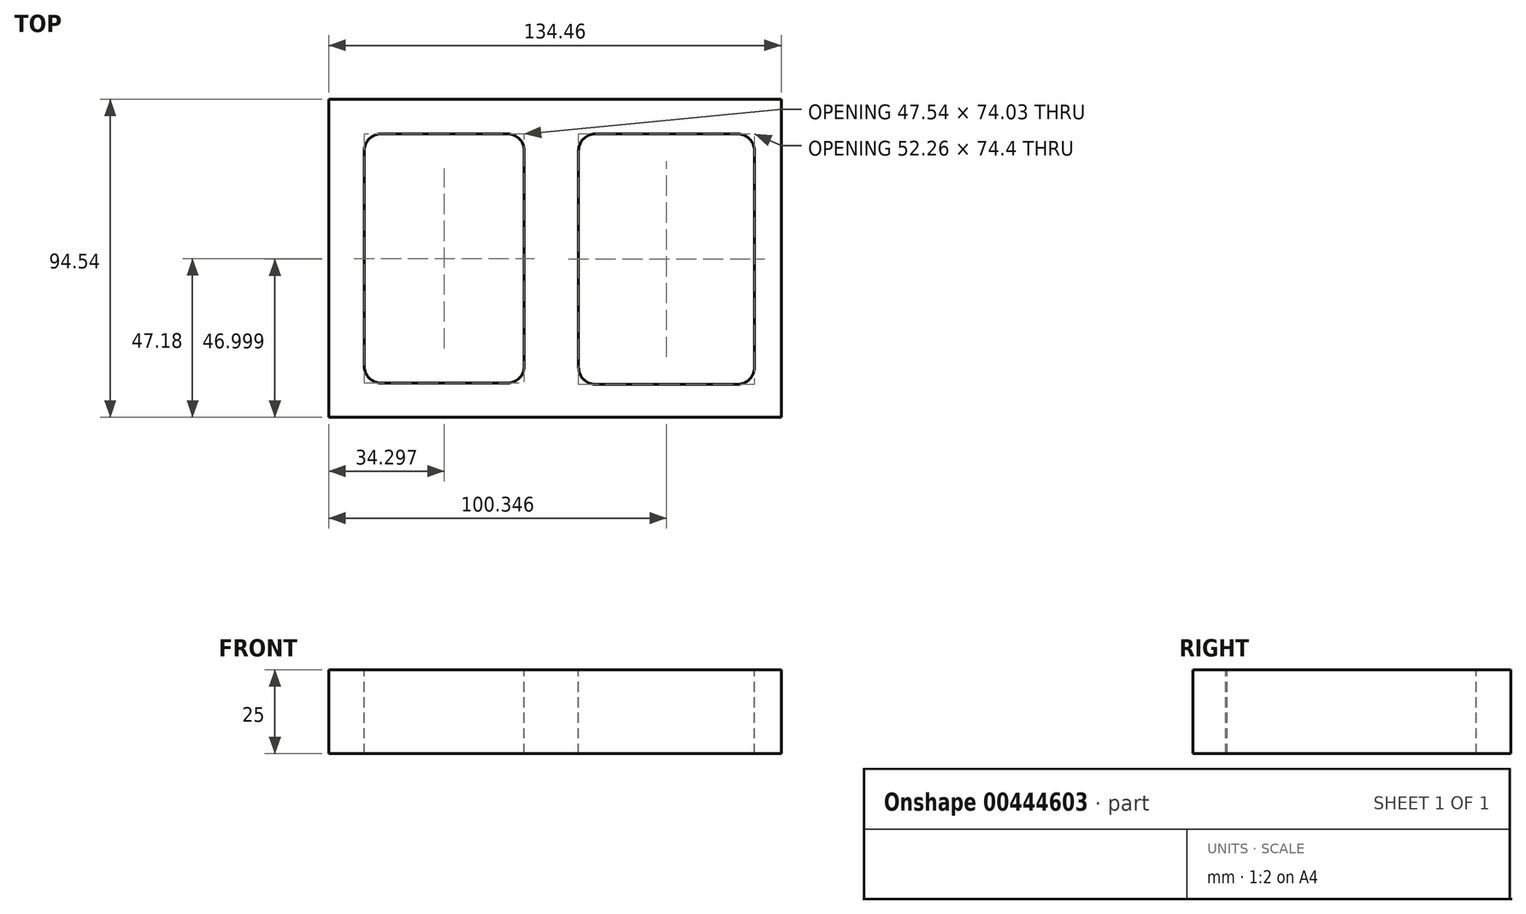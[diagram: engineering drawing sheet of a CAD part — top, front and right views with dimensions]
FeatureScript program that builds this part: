
annotation { "Feature Type Name" : "Feature", "Feature Type Description" : "" }
export const myFeature = defineFeature(function(context is Context, id is Id, definition is map)
    precondition{}
    {
        {
            var Q0;
            Q0=qCreatedBy(makeId("Top.planeOp"),FACE);
            var sketch = newSketch(context, id + "F0", { "sketchPlane" : qUnion([Q0])});
            skLineSegment(sketch, "E0.bottom", {"start": v(-67.14, 47.36) * mm, "end": v(67.32, 47.36) * mm});
            skLineSegment(sketch, "E0.top", {"start": v(-67.14, -47.18) * mm, "end": v(67.32, -47.18) * mm});
            skLineSegment(sketch, "E0.left", {"start": v(-67.14, 47.36) * mm, "end": v(-67.14, -47.18) * mm});
            skLineSegment(sketch, "E0.right", {"start": v(67.32, 47.36) * mm, "end": v(67.32, -47.18) * mm});
            skSolve(sketch);
        }
        {
            var Q0;
            Q0=makeQuery(id+"F0.imprint","IMPRINT",FACE,{"disambiguationData":[TD([[makeQuery(id+"F0.imprint","IMPRINT",EDGE,{"derivedFrom":sQuery(id+"F0.wireOp",EDGE,"E0.bottom")}),-1.0]])]});
            extrude(context, id + "F1", {"entities" : qUnion([Q0]), "depth" : 25 * mm});
        }
        {
            var Q0;
            Q0=makeQuery(id+"F1.opExtrude","CAP_FACE",FACE,{"disambiguationData":[OSD([sQuery(id+"F0.wireOp",EDGE,"E0.bottom"),sQuery(id+"F0.wireOp",EDGE,"E0.top"),sQuery(id+"F0.wireOp",EDGE,"E0.left"),sQuery(id+"F0.wireOp",EDGE,"E0.right")])],"isStart":false});
            var sketch = newSketch(context, id + "F2", { "sketchPlane" : qUnion([Q0])});
            skLineSegment(sketch, "E1.bottom", {"start": v(-56.61, 37.02) * mm, "end": v(-9.07, 37.02) * mm});
            skLineSegment(sketch, "E1.top", {"start": v(-56.61, -37.02) * mm, "end": v(-9.07, -37.02) * mm});
            skLineSegment(sketch, "E1.left", {"start": v(-56.61, 37.02) * mm, "end": v(-56.61, -37.02) * mm});
            skLineSegment(sketch, "E1.right", {"start": v(-9.07, 37.02) * mm, "end": v(-9.07, -37.02) * mm});
            skLineSegment(sketch, "E2.bottom", {"start": v(7.08, 37.02) * mm, "end": v(59.33, 37.02) * mm});
            skLineSegment(sketch, "E2.top", {"start": v(7.08, -37.38) * mm, "end": v(59.33, -37.38) * mm});
            skLineSegment(sketch, "E2.left", {"start": v(7.08, 37.02) * mm, "end": v(7.08, -37.38) * mm});
            skLineSegment(sketch, "E2.right", {"start": v(59.33, 37.02) * mm, "end": v(59.33, -37.38) * mm});
            skSolve(sketch);
        }
        {
            var Q0;
            Q0=makeQuery(id+"F2.imprint","IMPRINT",FACE,{"disambiguationData":[TD([[makeQuery(id+"F2.imprint","IMPRINT",EDGE,{"derivedFrom":sQuery(id+"F2.wireOp",EDGE,"E1.bottom")}),-1.0]])]});
            extrude(context, id + "F3", {"entities" : qUnion([Q0]), "operationType" : NewBodyOperationType.REMOVE, "oppositeDirection" : true, "depth" : 25 * mm});
        }
        {
            var Q0;
            Q0 = qSketchRegion(id + "F2", true);
            extrude(context, id + "F4", {"entities" : qUnion([Q0]), "operationType" : NewBodyOperationType.REMOVE, "oppositeDirection" : true, "depth" : 25 * mm});
        }
        {
            var Q0;
            Q0=makeQuery(id+"F3.boolean.opBoolean","COPY",EDGE,{"derivedFrom":makeQuery(id+"F3.opExtrude","SWEPT_EDGE",EDGE,{"disambiguationData":[OSD([sQuery(id+"F2.wireOp",EDGE,"E1.bottom"),sQuery(id+"F2.wireOp",EDGE,"E1.left")])]})});
            var Q1;
            Q1=makeQuery(id+"F3.boolean.opBoolean","COPY",EDGE,{"derivedFrom":makeQuery(id+"F3.opExtrude","SWEPT_EDGE",EDGE,{"disambiguationData":[OSD([sQuery(id+"F2.wireOp",EDGE,"E1.bottom"),sQuery(id+"F2.wireOp",EDGE,"E1.right")])]})});
            var Q2;
            Q2=makeQuery(id+"F3.boolean.opBoolean","COPY",EDGE,{"derivedFrom":makeQuery(id+"F3.opExtrude","SWEPT_EDGE",EDGE,{"disambiguationData":[OSD([sQuery(id+"F2.wireOp",EDGE,"E1.top"),sQuery(id+"F2.wireOp",EDGE,"E1.left")])]})});
            var Q3;
            Q3=makeQuery(id+"F3.boolean.opBoolean","COPY",EDGE,{"derivedFrom":makeQuery(id+"F3.opExtrude","SWEPT_EDGE",EDGE,{"disambiguationData":[OSD([sQuery(id+"F2.wireOp",EDGE,"E1.top"),sQuery(id+"F2.wireOp",EDGE,"E1.right")])]})});
            var Q4;
            Q4=makeQuery(id+"F4.boolean.opBoolean","COPY",EDGE,{"derivedFrom":makeQuery(id+"F4.opExtrude","SWEPT_EDGE",EDGE,{"disambiguationData":[OSD([sQuery(id+"F2.wireOp",EDGE,"E2.top"),sQuery(id+"F2.wireOp",EDGE,"E2.left")])]})});
            var Q5;
            Q5=makeQuery(id+"F4.boolean.opBoolean","COPY",EDGE,{"derivedFrom":makeQuery(id+"F4.opExtrude","SWEPT_EDGE",EDGE,{"disambiguationData":[OSD([sQuery(id+"F2.wireOp",EDGE,"E2.bottom"),sQuery(id+"F2.wireOp",EDGE,"E2.left")])]})});
            var Q6;
            Q6=makeQuery(id+"F4.boolean.opBoolean","COPY",EDGE,{"derivedFrom":makeQuery(id+"F4.opExtrude","SWEPT_EDGE",EDGE,{"disambiguationData":[OSD([sQuery(id+"F2.wireOp",EDGE,"E2.bottom"),sQuery(id+"F2.wireOp",EDGE,"E2.right")])]})});
            var Q7;
            Q7=makeQuery(id+"F4.boolean.opBoolean","COPY",EDGE,{"derivedFrom":makeQuery(id+"F4.opExtrude","SWEPT_EDGE",EDGE,{"disambiguationData":[OSD([sQuery(id+"F2.wireOp",EDGE,"E2.top"),sQuery(id+"F2.wireOp",EDGE,"E2.right")])]})});
            fillet(context, id + "F5", {"entities" : qUnion([Q0, Q1, Q2, Q3, Q4, Q5, Q6, Q7]), "radius" : 5 * mm, "tangentPropagation" : true, "allowEdgeOverflow" : false});
        }
    });
